# Revit family: QF_ELECTROLUXPROFESSIONAL_206378_WTNWTCT9E
name_source: partatom
category: Specialty Equipment
units: mm (PartAtom-declared; Revit-internal decimal feet)

## family parameters
Always vertical = Yes
Cut with Voids When Loaded = No
Enable Cutting in Views = No
Maintain Annotation Orientation = No
Part Type = Normal
Room Calculation Point = No
Round Connector Dimension = Use Diameter
Shared = No
Work Plane-Based = No

## types (1)
- QF_ELECTROLUXPROFESSIONAL_206378_WTNWTCT9E
    Accessory = No
    Cold Water Size = 1"
    Cycle = 50 Hz
    Default Elevation = 0 mm  [stored 0 ft]
    Depth Actual = 930 mm  [stored 3.05118 ft]
    Description = WORKTOP 200MM+WATER COLUMN+LT COUNT-900
    Direct Waste Size = 0"
    Gas Connection Height = 0 mm  [stored 0 ft]
    Gas Size = 1"
    HP = 0.3 HP
    Height Actual = 250 mm  [stored 0.82021 ft]
    Length Actual = 200 mm  [stored 0.656168 ft]
    Manufacturer = Electrolux Professional
    Model = WTNWTCT9E
    Phase = 1
    URL = http://www.electroluxprofessional.com
    URL Cutsheet = http://professional.electrolux.com
    URL Manufacturer = http://www.electroluxprofessional.com
    Volts = 230 V
    Watts = 0 W
    Weight = 13.00 kg
    Weight in Pounds = 115

note: [stored X ft] marks values corroborated as IEEE doubles in the binary element streams (Revit-internal decimal feet)

## geometry (parser evidence)
native form markers: Blend x8, Sweep x1
no freeform markers — native parametric forms only
